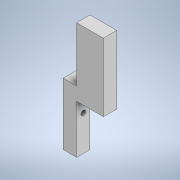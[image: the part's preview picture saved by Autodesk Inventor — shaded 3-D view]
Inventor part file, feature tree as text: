
AUTODESK INVENTOR PART (.ipt)
format: ipt  version: 2020.2 (Build 242310000, 310)  size: 137,728 bytes
history: native  units: mm
features: sketch x6, extrude x5, hole x1, projected_geometry x1
ambient origin geometry x8: Origin, YZ Plane, XZ Plane, XY Plane, X Axis, Y Axis, Z Axis, Center Point
bodies: Solid1 (feature_tree)
feature tree (13):
  extrude  "Extrusion1"  Depth=36.2mm
  hole  "Hole2"  [1 undecoded]
  extrude  "Extrusion2"  Depth=10.0mm TaperAngle=0.0deg
  extrude  "Extrusion3"  Depth=10.0mm
  extrude  "Extrusion4"  Depth=50.8mm TaperAngle=0.0deg
  extrude  "Extrusion5"  [1 undecoded]
  sketch  "Sketch1"  dims[d0=10.0mm d1=36.2mm]
  sketch  "Sketch3"  dims[d2=10.0mm d3=0.0mm d12=10.0mm]
  sketch  "Sketch4"  dims[d13=3.6mm d14=6.0mm d15=6.3mm d16=2.0mm d17=90.0deg d18=8.0mm d19=20.594885mm d20=10.0mm d21=0.0mm]
  sketch  "Sketch5"  dims[d22=10.0mm d23=10.0mm]
  sketch  "Sketch6"  dims[d24=20.0mm d25=0.0mm d26=50.8mm d27=0.0mm]
  sketch  "Sketch7"  dims[d28=10.0mm d29=0.0mm]
  projected_geometry  "Projected Loop1"
note: 2 required parameter values undecoded (feature->parameter linkage not recoverable at this tier; creation-order binding heuristic only, values carry confidence <= 0.55)
